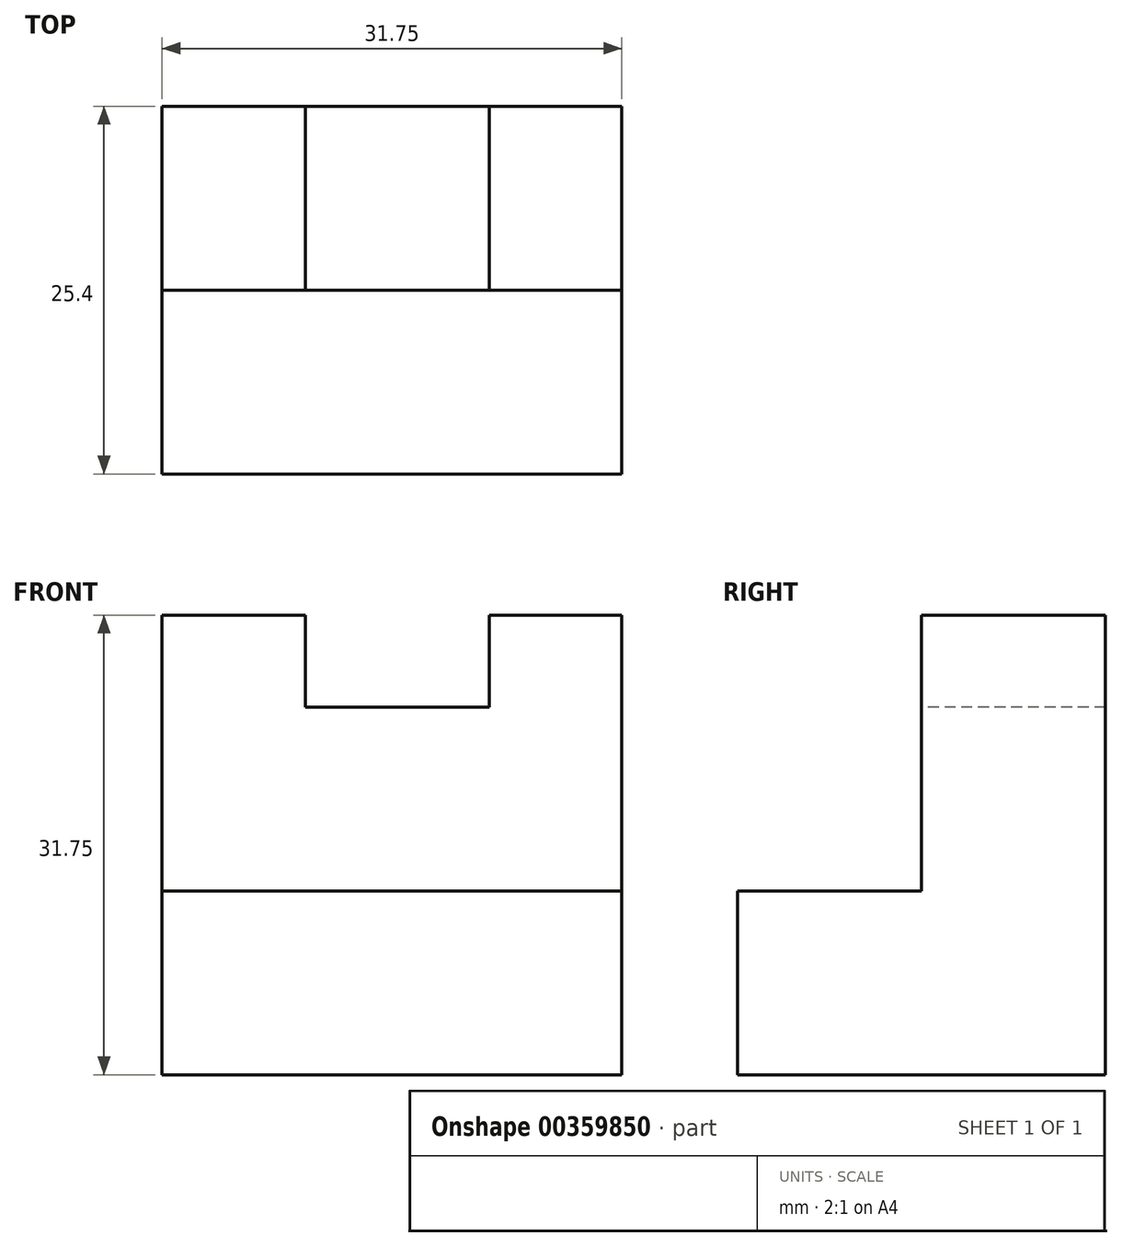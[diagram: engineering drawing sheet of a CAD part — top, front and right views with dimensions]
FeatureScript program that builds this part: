
annotation { "Feature Type Name" : "Feature", "Feature Type Description" : "" }
export const myFeature = defineFeature(function(context is Context, id is Id, definition is map)
    precondition{}
    {
        {
            var Q0;
            Q0=qCreatedBy(makeId("Right.planeOp"),FACE);
            var sketch = newSketch(context, id + "F0", { "sketchPlane" : qUnion([Q0])});
            skLineSegment(sketch, "E0", {"start": v(0, 0) * mm, "end": v(25.4, 0) * mm});
            skLineSegment(sketch, "E1", {"start": v(25.4, 31.75) * mm, "end": v(12.7, 31.75) * mm});
            skLineSegment(sketch, "E2", {"start": v(12.7, 31.75) * mm, "end": v(12.7, 12.7) * mm});
            skLineSegment(sketch, "E3", {"start": v(12.7, 12.7) * mm, "end": v(0, 12.7) * mm});
            skLineSegment(sketch, "E4", {"start": v(0, 12.7) * mm, "end": v(0, 3) * mm});
            skLineSegment(sketch, "E5", {"start": v(0, 3) * mm, "end": v(0, 0) * mm});
            skLineSegment(sketch, "E6", {"start": v(25.4, 0) * mm, "end": v(25.4, 31.75) * mm});
            skSolve(sketch);
        }
        {
            var Q0;
            Q0 = qSketchRegion(id + "F0", true);
            extrude(context, id + "F1", {"entities" : qUnion([Q0]), "depth" : 31.75 * mm});
        }
        {
            var Q0;
            Q0=makeQuery(id+"F1.opExtrude","SWEPT_FACE",FACE,{"disambiguationData":[OSD([sQuery(id+"F0.wireOp",EDGE,"E1")])]});
            var sketch = newSketch(context, id + "F2", { "sketchPlane" : qUnion([Q0])});
            skLineSegment(sketch, "E7", {"start": v(9.9, 25.4) * mm, "end": v(9.9, 12.7) * mm});
            skLineSegment(sketch, "E8", {"start": v(9.9, 12.7) * mm, "end": v(22.6, 12.7) * mm});
            skLineSegment(sketch, "E9", {"start": v(22.6, 12.7) * mm, "end": v(22.6, 25.4) * mm});
            skLineSegment(sketch, "E10", {"start": v(22.6, 25.4) * mm, "end": v(9.9, 25.4) * mm});
            skSolve(sketch);
        }
        {
            var Q0;
            Q0=makeQuery(id+"F2.imprint","IMPRINT",FACE,{"disambiguationData":[TD([[makeQuery(id+"F2.imprint","IMPRINT",EDGE,{"derivedFrom":sQuery(id+"F2.wireOp",EDGE,"E7")}),1.0]])]});
            extrude(context, id + "F3", {"entities" : qUnion([Q0]), "operationType" : NewBodyOperationType.REMOVE, "oppositeDirection" : true, "depth" : 6.35 * mm});
        }
    });
